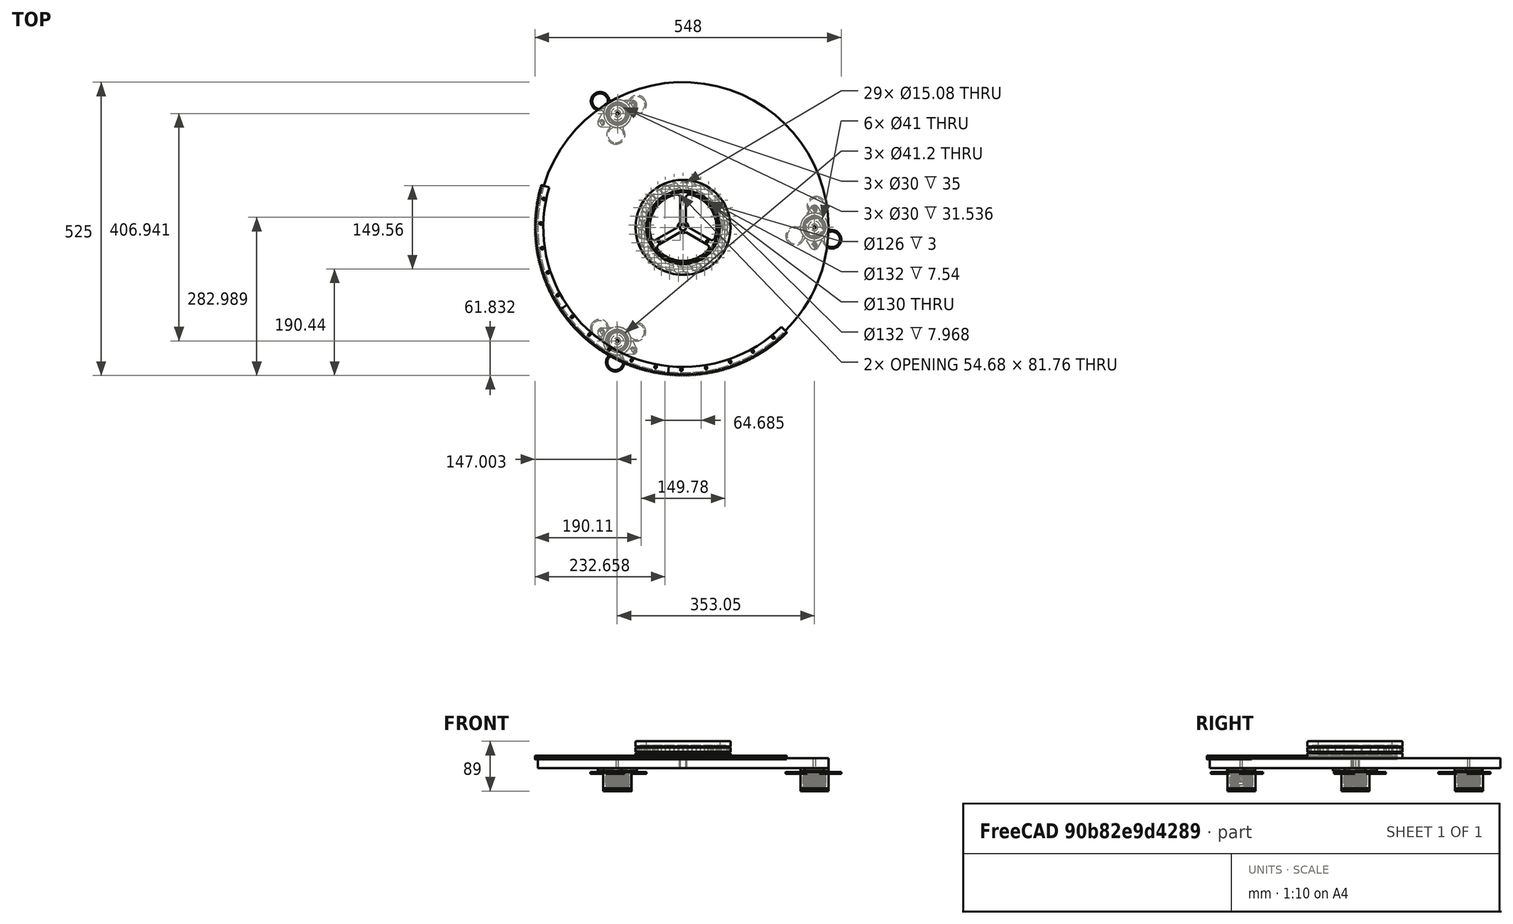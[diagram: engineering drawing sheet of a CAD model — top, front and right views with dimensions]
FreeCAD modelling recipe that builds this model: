
FCSTD DOCUMENT  (FreeCAD 2020.12.13R23076 +3015 (Git))
Label: zawieszenie-dol
License: All rights reserved
LicenseURL: http://en.wikipedia.org/wiki/All_rights_reserved
objects: App::FeaturePython×64, Part::FeaturePython×34, App::Link×12, App::LinkElement×6
note: 33 computed .brp shape members not serialized (recipe doc carries the construction recipe); baked Part::Feature solids carry a one-line shape summary decoded from their .brp
EXTERNAL_REF file=plyta-okr-dol.fcstd obj=Body
EXTERNAL_REF file=stopa.fcstd obj=Body
EXTERNAL_REF file=wieniec_mod1.FCStd obj=Body
EXTERNAL_REF file=tulejka-sruby.FCStd obj=Body
EXTERNAL_REF file=piasta-lozyska.FCStd obj=Body
EXTERNAL_REF file=lozysko 51126.FCStd obj=Assembly
EXTERNAL_REF file=regulacja-nogi.FCStd obj=Assembly

FEATURE [App::Link] Link  label="Link_plyta-okr-dol"
  LinkedObject = -> <external plyta-okr-dol.fcstd>#Body
  SyncGroupVisibility = false
  _LinkVersion = 1
FEATURE [App::Link] Link001  label="Link001_Assembly"
  LinkedObject = -> Assembly
  SyncGroupVisibility = false
  _LinkVersion = 1
FEATURE [App::Link] Link002  label="Link002_stopa"
  LinkPlacement = pos=(235,0,0) rot=(0,0,1;0rad)
  LinkedObject = -> <external stopa.fcstd>#Body
  Placement = pos=(235,0,0) rot=(0,0,1;0rad)
  SyncGroupVisibility = false
  _LinkVersion = 1
FEATURE [App::Link] Link003  label="Link003_Assembly"
  LinkedObject = -> Assembly
  SyncGroupVisibility = false
  _LinkVersion = 1
FEATURE [App::Link] Link004  label="Link004_Assembly"
  LinkedObject = -> Assembly
  SyncGroupVisibility = false
  _LinkVersion = 1
FEATURE [App::Link] Link005  label="Link005_stopa"
  LinkPlacement = pos=(-117.5,203.516,0) rot=(0,0,1;0rad)
  LinkedObject = -> <external stopa.fcstd>#Body
  Placement = pos=(-117.5,203.516,0) rot=(0,0,1;0rad)
  SyncGroupVisibility = false
  _LinkVersion = 1
FEATURE [App::Link] Link006  label="Link006_stopa"
  LinkPlacement = pos=(-117.5,-203.516,0) rot=(0,0,1;0rad)
  LinkedObject = -> <external stopa.fcstd>#Body
  Placement = pos=(-117.5,-203.516,0) rot=(0,0,1;0rad)
  SyncGroupVisibility = false
  _LinkVersion = 1
FEATURE [App::Link] Link008  label="tulejka-sruby"
  LinkPlacement = pos=(0,0,-4.40707e-10) rot=(0,0,1;0rad)
  LinkedObject = -> <external tulejka-sruby.FCStd>#Body
  Placement = pos=(0,0,-4.40707e-10) rot=(0,0,1;0rad)
  SyncGroupVisibility = false
  _LinkVersion = 1
FEATURE [App::Link] Link009  label="piasta-lozyska"
  LinkPlacement = pos=(0,0,18) rot=(0,0,1;0rad)
  LinkedObject = -> <external piasta-lozyska.FCStd>#Body
  Placement = pos=(0,0,18) rot=(0,0,1;0rad)
  SyncGroupVisibility = false
  _LinkVersion = 1
FEATURE [App::Link] Link010  label="51126-lozysko"
  LinkPlacement = pos=(0,0,18) rot=(0,-1,0;1.5708rad)
  LinkedObject = -> <external lozysko 51126.FCStd>#Assembly
  Placement = pos=(0,0,18) rot=(0,-1,0;1.5708rad)
  SyncGroupVisibility = false
  _LinkVersion = 1
FEATURE [App::LinkElement] Link011_i0
  LinkPlacement = pos=(0,0,1.8261e-12) rot=(0,0,1;0rad)
  LinkedObject = -> <external regulacja-nogi.FCStd>#Assembly
  Placement = pos=(0,0,1.8261e-12) rot=(0,0,1;0rad)
  _LinkVersion = 1
FEATURE [App::LinkElement] Link011_i1
  LinkPlacement = pos=(-203.516,-352.5,1.8296e-12) rot=(0,0,-1;1.0472rad)
  LinkedObject = -> <external regulacja-nogi.FCStd>#Assembly
  Placement = pos=(-203.516,-352.5,1.8296e-12) rot=(0,0,-1;1.0472rad)
  _LinkVersion = 1
FEATURE [App::LinkElement] Link011_i2
  LinkPlacement = pos=(203.516,-352.5,1.8296e-12) rot=(0,0,1;1.0472rad)
  LinkedObject = -> <external regulacja-nogi.FCStd>#Assembly
  Placement = pos=(203.516,-352.5,1.8296e-12) rot=(0,0,1;1.0472rad)
  _LinkVersion = 1
FEATURE [App::Link] Link011  label="regulacja-nogi"
  ElementCount = 3
  ElementList = -> [Link011_i0,Link011_i1,Link011_i2]
  LinkPlacement = pos=(235,0,-20) rot=(0.707107,0.707107,0;3.14159rad)
  LinkedObject = -> <external regulacja-nogi.FCStd>#Assembly
  Placement = pos=(235,0,-20) rot=(0.707107,0.707107,0;3.14159rad)
  SyncGroupVisibility = false
  _LinkVersion = 1
FEATURE [App::LinkElement] Link007_i0
  LinkPlacement = pos=(0,0,-3.6e-15) rot=(0,0,-1;5.65256rad)
  LinkedObject = -> <external wieniec_mod1.FCStd>#Body
  Placement = pos=(0,0,-3.6e-15) rot=(0,0,-1;5.65256rad)
  _LinkVersion = 0
FEATURE [App::LinkElement] Link007_i1
  LinkPlacement = pos=(2e-16,8e-16,3.6e-15) rot=(0,0,-1;4.77196rad)
  LinkedObject = -> <external wieniec_mod1.FCStd>#Body
  Placement = pos=(2e-16,8e-16,3.6e-15) rot=(0,0,-1;4.77196rad)
  _LinkVersion = 0
FEATURE [App::LinkElement] Link007_i2
  LinkPlacement = pos=(-1.93e-14,2.3e-15,2.49e-14) rot=(0,0,-1;0.249973rad)
  LinkedObject = -> <external wieniec_mod1.FCStd>#Body
  Placement = pos=(-1.93e-14,2.3e-15,2.49e-14) rot=(0,0,-1;0.249973rad)
  _LinkVersion = 0
FEATURE [App::Link] Link007  label="wieniec"
  ElementCount = 3
  ElementList = -> [Link007_i0,Link007_i1,Link007_i2]
  LinkPlacement = pos=(0,0,22) rot=(0.991445,-0.130526,0;3.14159rad)
  LinkedObject = -> <external wieniec_mod1.FCStd>#Body
  Placement = pos=(0,0,22) rot=(0.991445,-0.130526,0;3.14159rad)
  SyncGroupVisibility = false
  _LinkVersion = 1
FEATURE [Part::FeaturePython] Parts  # WARN: FeaturePython — macro-defined, semantics opaque (R4)
  Group = -> [Link,Link002,Link005,Link006,Link007,Link008,Link009,Link010,Link011]
  GroupMode = 0
  _LinkVersion = 1
FEATURE [Part::FeaturePython] Assembly  label="zawieszenie-dol"  # WARN: FeaturePython — macro-defined, semantics opaque (R4)
  AutoRelax = true
  BuildShape = 0
  Freeze = true
  Group = -> [Constraints,Elements,Parts]
  Verbose = false
  _LinkVersion = 1
  _SolverType = 1
FEATURE [App::FeaturePython] Constraints  # WARN: FeaturePython — macro-defined, semantics opaque (R4)
  Group = -> [Constraint001,Constraint002,Constraint003,Constraint004,Constraint005,Constraint006,Constraint,Constraint011,Constraint012,Constraint013,Constraint014,Constraint015,Constraint016,Constraint017,Constraint018,Constraint019,Constraint020,Constraint021,Constraint022,Constraint023,Constraint024]
  _LinkVersion = 1
  _Version = 1
FEATURE [App::FeaturePython] Elements  # WARN: FeaturePython — macro-defined, semantics opaque (R4)
  Group = -> [_Element,_Element001,_Element002,_Element003,_Element004,_Element005,_Element006,_Element007,_Element008,_Element009,_Element011,_Element013,_Element015,_Element017,Element,Element001,_Element018,_Element019,_Element020,_Element021,_Element022,_Element023,_Element024,_Element025,_Element026,_Element027,_Element028,_Element029,_Element030,_Element031,_Element032,_Element033]
  _LinkVersion = 1
FEATURE [Part::FeaturePython] _Element  # link proxy (typed FeaturePython)
  Detach = false
  LinkTransform = true
  LinkedObject = -> Link [PolarPattern.Face2]
  _LinkVersion = 1
  _Parent = -> Elements
FEATURE [App::FeaturePython] Constraint001  label="AxialAlignment"  # WARN: FeaturePython — macro-defined, semantics opaque (R4)
  Angle = 0
  AnglePitch = 0
  AngleRoll = 0
  Disabled = false
  Group = -> [ElementLink001,ElementLink002]
  LockAngle = false
  Multiply = false
  _ConstraintType = 36
  _LinkVersion = 1
  _Parent = -> Constraints
FEATURE [App::FeaturePython] ElementLink001  label="_Element001"  # link proxy (typed FeaturePython)
  LinkTransform = true
  LinkedObject = -> _Element001
  _LinkVersion = 1
  _Parent = -> Constraint001
FEATURE [Part::FeaturePython] _Element001  # link proxy (typed FeaturePython)
  Detach = false
  LinkTransform = true
  LinkedObject = -> Link005 [Revolution.Edge1]
  _LinkVersion = 1
  _Parent = -> Elements
FEATURE [App::FeaturePython] ElementLink002  label="_Element002"  # link proxy (typed FeaturePython)
  LinkTransform = true
  LinkedObject = -> _Element002
  _LinkVersion = 1
  _Parent = -> Constraint001
FEATURE [Part::FeaturePython] _Element002  # link proxy (typed FeaturePython)
  Detach = false
  LinkTransform = true
  LinkedObject = -> Link [PolarPattern.Edge6]
  _LinkVersion = 1
  _Parent = -> Elements
FEATURE [App::FeaturePython] Constraint002  label="PlaneAlignment"  # WARN: FeaturePython — macro-defined, semantics opaque (R4)
  Angle = 0
  AnglePitch = 0
  AngleRoll = 0
  Cascade = false
  Disabled = false
  Group = -> [ElementLink003,ElementLink004]
  LockAngle = false
  _ConstraintType = 37
  _LinkVersion = 1
  _Parent = -> Constraints
FEATURE [App::FeaturePython] ElementLink003  label="_Element"  # link proxy (typed FeaturePython)
  LinkTransform = true
  LinkedObject = -> _Element
  _LinkVersion = 1
  _Parent = -> Constraint002
FEATURE [App::FeaturePython] ElementLink004  label="_Element003"  # link proxy (typed FeaturePython)
  LinkTransform = true
  LinkedObject = -> _Element003
  _LinkVersion = 1
  _Parent = -> Constraint002
FEATURE [Part::FeaturePython] _Element003  # link proxy (typed FeaturePython)
  Detach = false
  LinkTransform = true
  LinkedObject = -> Link005 [Revolution.Face1]
  _LinkVersion = 1
  _Parent = -> Elements
FEATURE [App::FeaturePython] Constraint003  label="AxialAlignment001"  # WARN: FeaturePython — macro-defined, semantics opaque (R4)
  Angle = 0
  AnglePitch = 0
  AngleRoll = 0
  Disabled = false
  Group = -> [ElementLink005,ElementLink006]
  LockAngle = false
  Multiply = false
  _ConstraintType = 36
  _LinkVersion = 1
  _Parent = -> Constraints
FEATURE [App::FeaturePython] ElementLink005  label="_Element004"  # link proxy (typed FeaturePython)
  LinkTransform = true
  LinkedObject = -> _Element004
  _LinkVersion = 1
  _Parent = -> Constraint003
FEATURE [Part::FeaturePython] _Element004  # link proxy (typed FeaturePython)
  Detach = false
  LinkTransform = true
  LinkedObject = -> Link006 [Revolution.Edge1]
  _LinkVersion = 1
  _Parent = -> Elements
FEATURE [App::FeaturePython] ElementLink006  label="_Element005"  # link proxy (typed FeaturePython)
  LinkTransform = true
  LinkedObject = -> _Element005
  _LinkVersion = 1
  _Parent = -> Constraint003
FEATURE [Part::FeaturePython] _Element005  # link proxy (typed FeaturePython)
  Detach = false
  LinkTransform = true
  LinkedObject = -> Link [PolarPattern.Edge4]
  _LinkVersion = 1
  _Parent = -> Elements
FEATURE [App::FeaturePython] Constraint004  label="PlaneAlignment001"  # WARN: FeaturePython — macro-defined, semantics opaque (R4)
  Angle = 0
  AnglePitch = 0
  AngleRoll = 0
  Cascade = false
  Disabled = false
  Group = -> [ElementLink007,ElementLink008]
  LockAngle = false
  _ConstraintType = 37
  _LinkVersion = 1
  _Parent = -> Constraints
FEATURE [App::FeaturePython] ElementLink007  label="_Element"  # link proxy (typed FeaturePython)
  LinkTransform = true
  LinkedObject = -> _Element
  _LinkVersion = 1
  _Parent = -> Constraint004
FEATURE [App::FeaturePython] ElementLink008  label="_Element006"  # link proxy (typed FeaturePython)
  LinkTransform = true
  LinkedObject = -> _Element006
  _LinkVersion = 1
  _Parent = -> Constraint004
FEATURE [Part::FeaturePython] _Element006  # link proxy (typed FeaturePython)
  Detach = false
  LinkTransform = true
  LinkedObject = -> Link006 [Revolution.Face1]
  _LinkVersion = 1
  _Parent = -> Elements
FEATURE [App::FeaturePython] Constraint005  label="AxialAlignment002"  # WARN: FeaturePython — macro-defined, semantics opaque (R4)
  Angle = 0
  AnglePitch = 0
  AngleRoll = 0
  Disabled = false
  Group = -> [ElementLink009,ElementLink010]
  LockAngle = false
  Multiply = false
  _ConstraintType = 36
  _LinkVersion = 1
  _Parent = -> Constraints
FEATURE [App::FeaturePython] ElementLink009  label="_Element007"  # link proxy (typed FeaturePython)
  LinkTransform = true
  LinkedObject = -> _Element007
  _LinkVersion = 1
  _Parent = -> Constraint005
FEATURE [Part::FeaturePython] _Element007  # link proxy (typed FeaturePython)
  Detach = false
  LinkTransform = true
  LinkedObject = -> Link002 [Revolution.Edge1]
  _LinkVersion = 1
  _Parent = -> Elements
FEATURE [App::FeaturePython] ElementLink010  label="_Element008"  # link proxy (typed FeaturePython)
  LinkTransform = true
  LinkedObject = -> _Element008
  _LinkVersion = 1
  _Parent = -> Constraint005
FEATURE [Part::FeaturePython] _Element008  # link proxy (typed FeaturePython)
  Detach = false
  LinkTransform = true
  LinkedObject = -> Link [PolarPattern.Edge5]
  _LinkVersion = 1
  _Parent = -> Elements
FEATURE [App::FeaturePython] Constraint006  label="PlaneAlignment002"  # WARN: FeaturePython — macro-defined, semantics opaque (R4)
  Angle = 0
  AnglePitch = 0
  AngleRoll = 0
  Cascade = false
  Disabled = false
  Group = -> [ElementLink011,ElementLink012]
  LockAngle = false
  _ConstraintType = 37
  _LinkVersion = 1
  _Parent = -> Constraints
FEATURE [App::FeaturePython] ElementLink011  label="_Element"  # link proxy (typed FeaturePython)
  LinkTransform = true
  LinkedObject = -> _Element
  _LinkVersion = 1
  _Parent = -> Constraint006
FEATURE [App::FeaturePython] ElementLink012  label="_Element009"  # link proxy (typed FeaturePython)
  LinkTransform = true
  LinkedObject = -> _Element009
  _LinkVersion = 1
  _Parent = -> Constraint006
FEATURE [Part::FeaturePython] _Element009  # link proxy (typed FeaturePython)
  Detach = false
  LinkTransform = true
  LinkedObject = -> Link002 [Revolution.Face1]
  _LinkVersion = 1
  _Parent = -> Elements
FEATURE [Part::FeaturePython] _Element011  # link proxy (typed FeaturePython)
  Detach = false
  LinkTransform = true
  LinkedObject = -> Link [PolarPattern.Face1]
  _LinkVersion = 1
  _Parent = -> Elements
FEATURE [Part::FeaturePython] _Element013  # link proxy (typed FeaturePython)
  Detach = false
  LinkTransform = true
  LinkedObject = -> Link [PolarPattern.Face3]
  _LinkVersion = 1
  _Parent = -> Elements
FEATURE [Part::FeaturePython] _Element015  # link proxy (typed FeaturePython)
  Detach = false
  LinkTransform = true
  LinkedObject = -> Link [Pocket001.Face1]
  _LinkVersion = 1
  _Parent = -> Elements
FEATURE [Part::FeaturePython] _Element017  # link proxy (typed FeaturePython)
  Detach = false
  LinkTransform = true
  LinkedObject = -> Link [Pocket001.Face3]
  _LinkVersion = 1
  _Parent = -> Elements
FEATURE [Part::FeaturePython] Element  # link proxy (typed FeaturePython)
  Detach = false
  LinkTransform = true
  LinkedObject = -> Link [Pocket001.Face5]
  _LinkVersion = 1
  _Parent = -> Elements
FEATURE [Part::FeaturePython] Element001  # link proxy (typed FeaturePython)
  Detach = false
  LinkTransform = true
  LinkedObject = -> Link [Pocket001.Edge5]
  _LinkVersion = 1
  _Parent = -> Elements
FEATURE [App::FeaturePython] Constraint  label="Locked"  # WARN: FeaturePython — macro-defined, semantics opaque (R4)
  Disabled = false
  Group = -> [ElementLink]
  _ConstraintType = 0
  _LinkVersion = 1
  _Parent = -> Constraints
FEATURE [App::FeaturePython] ElementLink  label="_Element018"  # link proxy (typed FeaturePython)
  LinkTransform = true
  LinkedObject = -> _Element018
  _LinkVersion = 1
  _Parent = -> Constraint
FEATURE [Part::FeaturePython] _Element018  # link proxy (typed FeaturePython)
  Detach = false
  LinkTransform = true
  LinkedObject = -> Link [Pocket001.Face2]
  _LinkVersion = 1
  _Parent = -> Elements
FEATURE [Part::FeaturePython] _Element019  # link proxy (typed FeaturePython)
  Detach = false
  LinkTransform = true
  LinkedObject = -> Link008 [Chamfer.Face1]
  _LinkVersion = 1
  _Parent = -> Elements
FEATURE [Part::FeaturePython] _Element020  # link proxy (typed FeaturePython)
  Detach = false
  LinkTransform = true
  LinkedObject = -> Link008 [Chamfer.Face3]
  _LinkVersion = 1
  _Parent = -> Elements
FEATURE [App::FeaturePython] Constraint011  label="PlaneCoincident"  # WARN: FeaturePython — macro-defined, semantics opaque (R4)
  Angle = 0
  AnglePitch = 0
  AngleRoll = 0
  Cascade = false
  Disabled = false
  Group = -> [ElementLink021,ElementLink022]
  LockAngle = false
  Multiply = false
  OffsetX = 0
  OffsetY = 0
  _ConstraintType = 35
  _LinkVersion = 1
  _Parent = -> Constraints
FEATURE [App::FeaturePython] ElementLink021  label="_Element021"  # link proxy (typed FeaturePython)
  LinkTransform = true
  LinkedObject = -> _Element021
  _LinkVersion = 1
  _Parent = -> Constraint011
FEATURE [Part::FeaturePython] _Element021  # link proxy (typed FeaturePython)
  Detach = false
  LinkTransform = true
  LinkedObject = -> Link009 [Pocket002.Face1]
  _LinkVersion = 1
  _Parent = -> Elements
FEATURE [App::FeaturePython] ElementLink022  label="_Element017"  # link proxy (typed FeaturePython)
  LinkTransform = true
  LinkedObject = -> _Element017
  _LinkVersion = 1
  _Parent = -> Constraint011
FEATURE [App::FeaturePython] Constraint012  label="PlaneCoincident001"  # WARN: FeaturePython — macro-defined, semantics opaque (R4)
  Angle = 0
  AnglePitch = 0
  AngleRoll = 0
  Cascade = false
  Disabled = false
  Group = -> [ElementLink023,ElementLink024]
  LockAngle = false
  Multiply = false
  OffsetX = 0
  OffsetY = 0
  _ConstraintType = 35
  _LinkVersion = 1
  _Parent = -> Constraints
FEATURE [App::FeaturePython] ElementLink023  label="_Element020"  # link proxy (typed FeaturePython)
  LinkTransform = true
  LinkedObject = -> _Element020
  _LinkVersion = 1
  _Parent = -> Constraint012
FEATURE [App::FeaturePython] ElementLink024  label="_Element018"  # link proxy (typed FeaturePython)
  LinkTransform = true
  LinkedObject = -> _Element018
  _LinkVersion = 1
  _Parent = -> Constraint012
FEATURE [App::FeaturePython] Constraint013  label="PlaneCoincident002"  # WARN: FeaturePython — macro-defined, semantics opaque (R4)
  Angle = 0
  AnglePitch = 0
  AngleRoll = 0
  Cascade = false
  Disabled = false
  Group = -> [ElementLink025,ElementLink026]
  LockAngle = false
  Multiply = false
  OffsetX = 0
  OffsetY = 0
  _ConstraintType = 35
  _LinkVersion = 1
  _Parent = -> Constraints
FEATURE [App::FeaturePython] ElementLink025  label="_Element022"  # link proxy (typed FeaturePython)
  LinkTransform = true
  LinkedObject = -> _Element022
  _LinkVersion = 1
  _Parent = -> Constraint013
FEATURE [Part::FeaturePython] _Element022  # link proxy (typed FeaturePython)
  Detach = false
  LinkTransform = true
  LinkedObject = -> Link010 [1.$Element.]
  _LinkVersion = 1
  _Parent = -> Elements
FEATURE [App::FeaturePython] ElementLink026  label="_Element017"  # link proxy (typed FeaturePython)
  LinkTransform = true
  LinkedObject = -> _Element017
  _LinkVersion = 1
  _Parent = -> Constraint013
FEATURE [Part::FeaturePython] _Element023  # link proxy (typed FeaturePython)
  Detach = false
  LinkTransform = true
  LinkedObject = -> Link [Pocket001.Edge6]
  _LinkVersion = 1
  _Parent = -> Elements
FEATURE [App::FeaturePython] Constraint014  label="PlaneCoincident003"  # WARN: FeaturePython — macro-defined, semantics opaque (R4)
  Angle = 0
  AnglePitch = 0
  AngleRoll = 0
  Cascade = false
  Disabled = false
  Group = -> [ElementLink027,ElementLink028]
  LockAngle = false
  Multiply = false
  OffsetX = 0
  OffsetY = 0
  _ConstraintType = 35
  _LinkVersion = 1
  _Parent = -> Constraints
FEATURE [App::FeaturePython] ElementLink027  label="_Element024"  # link proxy (typed FeaturePython)
  LinkTransform = true
  LinkedObject = -> _Element024
  _LinkVersion = 1
  _Parent = -> Constraint014
FEATURE [Part::FeaturePython] _Element024  # link proxy (typed FeaturePython)
  Detach = false
  LinkTransform = true
  LinkedObject = -> Link011 [0.1.$Element002.]
  _LinkVersion = 1
  _Parent = -> Elements
FEATURE [App::FeaturePython] ElementLink028  label="_Element009"  # link proxy (typed FeaturePython)
  LinkTransform = true
  LinkedObject = -> _Element009
  _LinkVersion = 1
  _Parent = -> Constraint014
FEATURE [App::FeaturePython] Constraint015  label="PlaneCoincident004"  # WARN: FeaturePython — macro-defined, semantics opaque (R4)
  Angle = 0
  AnglePitch = 0
  AngleRoll = 0
  Cascade = false
  Disabled = false
  Group = -> [ElementLink029,ElementLink030]
  LockAngle = false
  Multiply = false
  OffsetX = 0
  OffsetY = 0
  _ConstraintType = 35
  _LinkVersion = 1
  _Parent = -> Constraints
FEATURE [App::FeaturePython] ElementLink029  label="_Element025"  # link proxy (typed FeaturePython)
  LinkTransform = true
  LinkedObject = -> _Element025
  _LinkVersion = 1
  _Parent = -> Constraint015
FEATURE [Part::FeaturePython] _Element025  # link proxy (typed FeaturePython)
  Detach = false
  LinkTransform = true
  LinkedObject = -> Link011 [2.1.$Element002.]
  _LinkVersion = 1
  _Parent = -> Elements
FEATURE [App::FeaturePython] ElementLink030  label="_Element003"  # link proxy (typed FeaturePython)
  LinkTransform = true
  LinkedObject = -> _Element003
  _LinkVersion = 1
  _Parent = -> Constraint015
FEATURE [App::FeaturePython] Constraint016  label="PlaneCoincident005"  # WARN: FeaturePython — macro-defined, semantics opaque (R4)
  Angle = 0
  AnglePitch = 0
  AngleRoll = 0
  Cascade = false
  Disabled = false
  Group = -> [ElementLink031,ElementLink032]
  LockAngle = false
  Multiply = false
  OffsetX = 0
  OffsetY = 0
  _ConstraintType = 35
  _LinkVersion = 1
  _Parent = -> Constraints
FEATURE [App::FeaturePython] ElementLink031  label="_Element006"  # link proxy (typed FeaturePython)
  LinkTransform = true
  LinkedObject = -> _Element006
  _LinkVersion = 1
  _Parent = -> Constraint016
FEATURE [App::FeaturePython] ElementLink032  label="_Element026"  # link proxy (typed FeaturePython)
  LinkTransform = true
  LinkedObject = -> _Element026
  _LinkVersion = 1
  _Parent = -> Constraint016
FEATURE [Part::FeaturePython] _Element026  # link proxy (typed FeaturePython)
  Detach = false
  LinkTransform = true
  LinkedObject = -> Link011 [1.1.$Element002.]
  _LinkVersion = 1
  _Parent = -> Elements
FEATURE [App::FeaturePython] Constraint017  label="AxialAlignment003"  # WARN: FeaturePython — macro-defined, semantics opaque (R4)
  Angle = 0
  AnglePitch = 0
  AngleRoll = 0
  Disabled = false
  Group = -> [ElementLink033,ElementLink034]
  LockAngle = false
  Multiply = false
  _ConstraintType = 36
  _LinkVersion = 0
  _Parent = -> Constraints
FEATURE [App::FeaturePython] ElementLink033  label="_Element027"  # link proxy (typed FeaturePython)
  LinkTransform = true
  LinkedObject = -> _Element027
  _LinkVersion = 0
  _Parent = -> Constraint017
FEATURE [Part::FeaturePython] _Element027  # link proxy (typed FeaturePython)
  Detach = false
  LinkTransform = true
  LinkedObject = -> Link007 [2.Pocket003.Face3]
  _LinkVersion = 0
  _Parent = -> Elements
FEATURE [App::FeaturePython] ElementLink034  label="_Element015"  # link proxy (typed FeaturePython)
  LinkTransform = true
  LinkedObject = -> _Element015
  _LinkVersion = 0
  _Parent = -> Constraint017
FEATURE [App::FeaturePython] Constraint018  label="AxialAlignment004"  # WARN: FeaturePython — macro-defined, semantics opaque (R4)
  Angle = 0
  AnglePitch = 0
  AngleRoll = 0
  Disabled = false
  Group = -> [ElementLink035,ElementLink036]
  LockAngle = false
  Multiply = false
  _ConstraintType = 36
  _LinkVersion = 0
  _Parent = -> Constraints
FEATURE [App::FeaturePython] ElementLink035  label="_Element028"  # link proxy (typed FeaturePython)
  LinkTransform = true
  LinkedObject = -> _Element028
  _LinkVersion = 0
  _Parent = -> Constraint018
FEATURE [Part::FeaturePython] _Element028  # link proxy (typed FeaturePython)
  Detach = false
  LinkTransform = true
  LinkedObject = -> Link007 [0.Pocket003.Face3]
  _LinkVersion = 0
  _Parent = -> Elements
FEATURE [App::FeaturePython] ElementLink036  label="_Element015"  # link proxy (typed FeaturePython)
  LinkTransform = true
  LinkedObject = -> _Element015
  _LinkVersion = 0
  _Parent = -> Constraint018
FEATURE [App::FeaturePython] Constraint019  label="PointInPlane"  # WARN: FeaturePython — macro-defined, semantics opaque (R4)
  Disabled = false
  Group = -> [ElementLink037,ElementLink038]
  _ConstraintType = 3
  _LinkVersion = 0
  _Parent = -> Constraints
FEATURE [App::FeaturePython] ElementLink037  label="_Element029"  # link proxy (typed FeaturePython)
  LinkTransform = true
  LinkedObject = -> _Element029
  _LinkVersion = 0
  _Parent = -> Constraint019
FEATURE [Part::FeaturePython] _Element029  # link proxy (typed FeaturePython)
  Detach = false
  LinkTransform = true
  LinkedObject = -> Link007 [0.Pocket003.Vertex323]
  _LinkVersion = 0
  _Parent = -> Elements
FEATURE [App::FeaturePython] ElementLink038  label="_Element017"  # link proxy (typed FeaturePython)
  LinkTransform = true
  LinkedObject = -> _Element017
  _LinkVersion = 0
  _Parent = -> Constraint019
FEATURE [App::FeaturePython] Constraint020  label="PointInPlane001"  # WARN: FeaturePython — macro-defined, semantics opaque (R4)
  Disabled = false
  Group = -> [ElementLink039,ElementLink040]
  _ConstraintType = 3
  _LinkVersion = 0
  _Parent = -> Constraints
FEATURE [App::FeaturePython] ElementLink039  label="_Element030"  # link proxy (typed FeaturePython)
  LinkTransform = true
  LinkedObject = -> _Element030
  _LinkVersion = 0
  _Parent = -> Constraint020
FEATURE [Part::FeaturePython] _Element030  # link proxy (typed FeaturePython)
  Detach = false
  LinkTransform = true
  LinkedObject = -> Link007 [2.Pocket003.Vertex325]
  _LinkVersion = 0
  _Parent = -> Elements
FEATURE [App::FeaturePython] ElementLink040  label="_Element017"  # link proxy (typed FeaturePython)
  LinkTransform = true
  LinkedObject = -> _Element017
  _LinkVersion = 0
  _Parent = -> Constraint020
FEATURE [App::FeaturePython] Constraint021  label="PointsCoincident"  # WARN: FeaturePython — macro-defined, semantics opaque (R4)
  Disabled = false
  Group = -> [ElementLink041,ElementLink042]
  _ConstraintType = 1
  _LinkVersion = 0
  _Parent = -> Constraints
FEATURE [App::FeaturePython] ElementLink041  label="_Element030"  # link proxy (typed FeaturePython)
  LinkTransform = true
  LinkedObject = -> _Element030
  _LinkVersion = 0
  _Parent = -> Constraint021
FEATURE [App::FeaturePython] ElementLink042  label="_Element029"  # link proxy (typed FeaturePython)
  LinkTransform = true
  LinkedObject = -> _Element029
  _LinkVersion = 0
  _Parent = -> Constraint021
FEATURE [App::FeaturePython] Constraint022  label="AxialAlignment005"  # WARN: FeaturePython — macro-defined, semantics opaque (R4)
  Angle = 0
  AnglePitch = 0
  AngleRoll = 0
  Disabled = false
  Group = -> [ElementLink043,ElementLink044]
  LockAngle = false
  Multiply = false
  _ConstraintType = 36
  _LinkVersion = 0
  _Parent = -> Constraints
FEATURE [App::FeaturePython] ElementLink043  label="_Element031"  # link proxy (typed FeaturePython)
  LinkTransform = true
  LinkedObject = -> _Element031
  _LinkVersion = 0
  _Parent = -> Constraint022
FEATURE [Part::FeaturePython] _Element031  # link proxy (typed FeaturePython)
  Detach = false
  LinkTransform = true
  LinkedObject = -> Link007 [1.Pocket003.Face3]
  _LinkVersion = 0
  _Parent = -> Elements
FEATURE [App::FeaturePython] ElementLink044  label="_Element015"  # link proxy (typed FeaturePython)
  LinkTransform = true
  LinkedObject = -> _Element015
  _LinkVersion = 0
  _Parent = -> Constraint022
FEATURE [App::FeaturePython] Constraint023  label="PointInPlane002"  # WARN: FeaturePython — macro-defined, semantics opaque (R4)
  Disabled = false
  Group = -> [ElementLink045,ElementLink046]
  _ConstraintType = 3
  _LinkVersion = 0
  _Parent = -> Constraints
FEATURE [App::FeaturePython] ElementLink045  label="_Element032"  # link proxy (typed FeaturePython)
  LinkTransform = true
  LinkedObject = -> _Element032
  _LinkVersion = 0
  _Parent = -> Constraint023
FEATURE [Part::FeaturePython] _Element032  # link proxy (typed FeaturePython)
  Detach = false
  LinkTransform = true
  LinkedObject = -> Link007 [1.Pocket003.Vertex323]
  _LinkVersion = 0
  _Parent = -> Elements
FEATURE [App::FeaturePython] ElementLink046  label="_Element017"  # link proxy (typed FeaturePython)
  LinkTransform = true
  LinkedObject = -> _Element017
  _LinkVersion = 0
  _Parent = -> Constraint023
FEATURE [App::FeaturePython] Constraint024  label="PointsCoincident001"  # WARN: FeaturePython — macro-defined, semantics opaque (R4)
  Disabled = false
  Group = -> [ElementLink047,ElementLink048]
  _ConstraintType = 1
  _LinkVersion = 0
  _Parent = -> Constraints
FEATURE [App::FeaturePython] ElementLink047  label="_Element032"  # link proxy (typed FeaturePython)
  LinkTransform = true
  LinkedObject = -> _Element032
  _LinkVersion = 0
  _Parent = -> Constraint024
FEATURE [App::FeaturePython] ElementLink048  label="_Element033"  # link proxy (typed FeaturePython)
  LinkTransform = true
  LinkedObject = -> _Element033
  _LinkVersion = 0
  _Parent = -> Constraint024
FEATURE [Part::FeaturePython] _Element033  # link proxy (typed FeaturePython)
  Detach = false
  LinkTransform = true
  LinkedObject = -> Link007 [0.Pocket003.Vertex325]
  _LinkVersion = 0
  _Parent = -> Elements

RESOLVED EXTERNAL PARTS (link-assembly join: the EXTERNAL_REF files above that resolve inside this repo's crawl, each included once):
---- part piasta-lozyska.FCStd = doc fcstd_be0ec29206c3 ----
FCSTD DOCUMENT  (FreeCAD 2020.10.16R22739 +2665 (Git))
Label: piasta-lozyska
License: All rights reserved
LicenseURL: http://en.wikipedia.org/wiki/All_rights_reserved
objects: Sketcher::SketchObject×4, PartDesign::Pocket×3, PartDesign::Pad×1, PartDesign::PolarPattern×1, PartDesign::Chamfer×1, PartDesign::Fillet×1, PartDesign::Body×1
note: 25 computed .brp shape members not serialized (recipe doc carries the construction recipe); baked Part::Feature solids carry a one-line shape summary decoded from their .brp

FEATURE [Sketcher::SketchObject] Sketch002
  MapMode = 5
  Support = -> [XY_Plane]
  sketch-geometry (7):
    g0: ArcOfCircle CenterX=0 CenterY=0 CenterZ=0 NormalX=0 NormalY=0 NormalZ=1 AngleXU=0 Radius=60 StartAngle=1.65423 EndAngle=3.58176
    g1: ArcOfCircle CenterX=0 CenterY=0 CenterZ=0 NormalX=0 NormalY=0 NormalZ=1 AngleXU=0 Radius=10 StartAngle=2.0944 EndAngle=3.14159
    g2: LineSegment StartX=-5 StartY=8.66025 StartZ=0 EndX=-5 EndY=59.7913 EndZ=0
    g3: LineSegment [constr] StartX=0 StartY=0 StartZ=0 EndX=-86.6025 EndY=-50 EndZ=0
    g4: LineSegment StartX=-10 StartY=-1e-16 StartZ=0 EndX=-54.2808 EndY=-25.5655 EndZ=0
    g5: LineSegment [constr] StartX=-10 StartY=-1e-16 StartZ=0 EndX=0 EndY=0 EndZ=0
    g6: Circle CenterX=0 CenterY=50 CenterZ=0 NormalX=0 NormalY=0 NormalZ=1 AngleXU=0 Radius=2
  constraints (20):
    c: Coincident(g0,g-1)
    c: Coincident(g1,g0)
    c: Vertical(g2)
    c: Coincident(g3,g0)
    c: Angle(g3) = -2.61799
    c: Parallel(g4,g3)
    c: Diameter(g0) = 120
    c: Coincident(g5,g4)
    c: Coincident(g5,g0)
    c: Coincident(g0,g2)
    c: Coincident(g0,g4)
    c: Coincident(g1,g2)
    c: DistanceX(g1) = -5
    c: Diameter(g1) = 20
    c: Distance(g1,g3) = 5
    c: Coincident(g4,g1)
    c: Distance(g3) = 100
    c: PointOnObject(g6,g-2)
    c: Diameter(g6) = 4
    c: DistanceY(g6) = 50
FEATURE [Sketcher::SketchObject] Sketch001
  MapMode = 5
  Support = -> [XY_Plane]
  sketch-geometry (1):
    g0: Circle CenterX=0 CenterY=0 CenterZ=0 NormalX=0 NormalY=0 NormalZ=1 AngleXU=0 Radius=5.5
  constraints (2):
    c: Coincident(g0,g-1)
    c: Diameter(g0) = 11
FEATURE [Sketcher::SketchObject] Sketch
  MapMode = 5
  Support = -> [XY_Plane]
  sketch-geometry (1):
    g0: Circle CenterX=0 CenterY=0 CenterZ=0 NormalX=0 NormalY=0 NormalZ=1 AngleXU=0 Radius=65.25
  constraints (2):
    c: Coincident(g0,g-1)
    c: Diameter(g0) = 130.5
FEATURE [PartDesign::Pad] Pad
  ClaimChildren = false
  Direction = (1,1,1)
  Length = 6
  Length2 = 100
  NewSolid = false
  Profile = -> Sketch
  Suppress = false
  Type = 0
FEATURE [PartDesign::Pocket] Pocket
  BaseFeature = -> Pad
  ClaimChildren = false
  Length = 5
  Length2 = 100
  NewSolid = false
  Profile = -> Sketch001
  Reversed = true
  Suppress = false
  Type = 1
FEATURE [PartDesign::Pocket] Pocket001
  BaseFeature = -> Pocket
  ClaimChildren = false
  Length = 5
  Length2 = 100
  NewSolid = false
  Profile = -> Sketch002
  Reversed = true
  Suppress = false
  Type = 1
FEATURE [PartDesign::PolarPattern] PolarPattern
  Angle = 360
  Axis = -> Sketch002 [N_Axis]
  BaseFeature = -> Pocket001
  CopyShape = false
  NewSolid = false
  Occurrences = 3
  OriginalSubs = -> [Pocket001]
  Originals = -> [Pocket001]
  SubTransform = true
  Suppress = false
FEATURE [PartDesign::Chamfer] Chamfer
  Angle = 45
  Base = -> PolarPattern [Edge3,Edge2]
  BaseFeature = -> PolarPattern
  ChamferType = 0
  FlipDirection = false
  NewSolid = false
  Size = 1
  Size2 = 1
  SupportTransform = true
  Suppress = false
FEATURE [PartDesign::Fillet] Fillet
  Base = -> Chamfer [Edge49,Edge46,Edge54,Edge52,Edge42,Edge40]
  BaseFeature = -> Chamfer
  NewSolid = false
  Radius = 6
  SupportTransform = true
  Suppress = false
FEATURE [Sketcher::SketchObject] Sketch003
  MapMode = 5
  Placement = pos=(0,0,6) rot=(0,0,1;0rad)
  Support = -> [Fillet]
  sketch-geometry (1):
    g0: Circle CenterX=0 CenterY=0 CenterZ=0 NormalX=0 NormalY=0 NormalZ=1 AngleXU=0 Radius=63
  constraints (2):
    c: Coincident(g0,g-1)
    c: Diameter(g0) = 126
FEATURE [PartDesign::Pocket] Pocket002
  BaseFeature = -> Fillet
  ClaimChildren = false
  Length = 3
  Length2 = 100
  NewSolid = false
  Profile = -> Sketch003
  Suppress = false
  Type = 0
FEATURE [PartDesign::Body] Body  label="piasta-lozyska"
  ExportMode = 0
  Group = -> [Sketch,Pad,Sketch001,Pocket,Sketch002,Pocket001,PolarPattern,Chamfer,Fillet,Sketch003,Pocket002]
  Origin = -> Origin
  Tip = -> Pocket002
  _ExportChildren = -> [Pad,Pocket,Pocket001,PolarPattern,Chamfer,Fillet,Pocket002]
  _GroupVersion = 1
---- part plyta-okr-dol.fcstd = doc fcstd_a5daffcc101f ----
FCSTD DOCUMENT  (FreeCAD 2020.12.13R23076 +3015 (Git))
Label: plyta-okr-dol
License: All rights reserved
LicenseURL: http://en.wikipedia.org/wiki/All_rights_reserved
objects: Sketcher::SketchObject×3, PartDesign::Pocket×2, PartDesign::Pad×1, PartDesign::PolarPattern×1, PartDesign::Body×1
note: 15 computed .brp shape members not serialized (recipe doc carries the construction recipe); baked Part::Feature solids carry a one-line shape summary decoded from their .brp

FEATURE [Sketcher::SketchObject] Sketch
  MapMode = 5
  Support = -> [XY_Plane]
  sketch-geometry (1):
    g0: Circle CenterX=0 CenterY=0 CenterZ=0 NormalX=0 NormalY=0 NormalZ=1 AngleXU=0 Radius=260
  constraints (2):
    c: Coincident(g0,g-1)
    c: Diameter(g0) = 520
FEATURE [PartDesign::Pad] Pad
  AllowMultiFace = false
  ClaimChildren = false
  Direction = (1,1,1)
  Fit = 0
  FitJoin = 0
  InnerFit = 0
  InnerFitJoin = 0
  InnerTaperAngle = 0
  InnerTaperAngleRev = 0
  Length = 18
  Length2 = 100
  NewSolid = false
  Profile = -> Sketch
  Suppress = false
  Type = 0
FEATURE [Sketcher::SketchObject] Sketch001
  MapMode = 5
  Placement = pos=(0,0,18) rot=(0,0,1;0rad)
  Support = -> [Pad]
  sketch-geometry (1):
    g0: Circle CenterX=235 CenterY=0 CenterZ=0 NormalX=0 NormalY=0 NormalZ=1 AngleXU=0 Radius=2
  constraints (3):
    c: PointOnObject(g0,g-1)
    c: DistanceX(g0) = 235
    c: Radius(g0) = 2
FEATURE [PartDesign::Pocket] Pocket
  AllowMultiFace = false
  BaseFeature = -> Pad
  ClaimChildren = false
  Fit = 0
  FitJoin = 0
  InnerFit = 0
  InnerFitJoin = 0
  InnerTaperAngle = 0
  InnerTaperAngleRev = 0
  Length = 5
  Length2 = 100
  NewSolid = false
  Profile = -> Sketch001
  Suppress = false
  Type = 1
FEATURE [PartDesign::PolarPattern] PolarPattern
  Angle = 360
  Axis = -> Sketch001 [N_Axis]
  BaseFeature = -> Pocket
  CopyShape = true
  NewSolid = false
  Occurrences = 3
  OriginalSubs = -> [Pocket]
  Originals = -> [Pocket]
  SubTransform = true
  Suppress = false
FEATURE [Sketcher::SketchObject] Sketch002
  MapMode = 5
  Support = -> [XY_Plane]
  sketch-geometry (1):
    g0: Circle CenterX=0 CenterY=0 CenterZ=0 NormalX=0 NormalY=0 NormalZ=1 AngleXU=0 Radius=7
  constraints (2):
    c: Coincident(g0,g-1)
    c: Diameter(g0) = 14
FEATURE [PartDesign::Pocket] Pocket001
  BaseFeature = -> PolarPattern
  ClaimChildren = false
  Fit = 0
  FitJoin = 0
  InnerFit = 0
  InnerFitJoin = 0
  InnerTaperAngle = 0
  InnerTaperAngleRev = 0
  Length = 5
  Length2 = 100
  NewSolid = false
  Profile = -> Sketch002
  Reversed = true
  Suppress = false
  Type = 1
FEATURE [PartDesign::Body] Body  label="plyta-okr-dol"
  ExportMode = 0
  Group = -> [Sketch,Pad,Sketch001,Pocket,PolarPattern,Sketch002,Pocket001]
  Origin = -> Origin
  SingleSolid = true
  Tip = -> Pocket001
  _ExportChildren = -> [Pad,Pocket,PolarPattern,Pocket001]
  _GroupVersion = 1
---- part regulacja-nogi.FCStd = doc fcstd_2b6e49dfca54 ----
FCSTD DOCUMENT  (FreeCAD 2020.11.29R23076 +2859 (Git))
Label: regulacja-nogi
License: All rights reserved
LicenseURL: http://en.wikipedia.org/wiki/All_rights_reserved
objects: App::FeaturePython×13, Part::FeaturePython×11, App::Link×3
note: 10 computed .brp shape members not serialized (recipe doc carries the construction recipe); baked Part::Feature solids carry a one-line shape summary decoded from their .brp
EXTERNAL_REF file=nakretka-rzymska.FCStd obj=Body
EXTERNAL_REF file=noga-gora.FCStd obj=Body
EXTERNAL_REF file=noga-dol.FCStd obj=Body

FEATURE [App::Link] Link  label="nakretka-rzymska"
  LinkPlacement = pos=(0.604474,0.0526819,2) rot=(0,0,1;0.086943rad)
  LinkedObject = -> <external nakretka-rzymska.FCStd>#Body
  Placement = pos=(0.604474,0.0526819,2) rot=(0,0,1;0.086943rad)
  SyncGroupVisibility = false
  _LinkVersion = 1
FEATURE [App::Link] Link001  label="noga-gora"
  LinkPlacement = pos=(0.604474,0.0526819,21) rot=(0,0,1;0.173886rad)
  LinkedObject = -> <external noga-gora.FCStd>#Body
  Placement = pos=(0.604474,0.0526819,21) rot=(0,0,1;0.173886rad)
  SyncGroupVisibility = false
  _LinkVersion = 1
FEATURE [App::Link] Link002  label="noga-dol"
  LinkPlacement = pos=(0,-5.76185e-06,-20) rot=(-1,0,0;3.14159rad)
  LinkedObject = -> <external noga-dol.FCStd>#Body
  Placement = pos=(0,-5.76185e-06,-20) rot=(-1,0,0;3.14159rad)
  SyncGroupVisibility = false
  _LinkVersion = 1
FEATURE [Part::FeaturePython] Parts  # WARN: FeaturePython — macro-defined, semantics opaque (R4)
  Group = -> [Link,Link001,Link002]
  GroupMode = 0
  _LinkVersion = 1
FEATURE [Part::FeaturePython] Assembly  label="regulacja-nogi"  # WARN: FeaturePython — macro-defined, semantics opaque (R4)
  AutoRelax = true
  BuildShape = 0
  Freeze = false
  Group = -> [Constraints,Elements,Parts]
  Verbose = false
  _LinkVersion = 1
  _SolverType = 1
  _Version = 1
FEATURE [App::FeaturePython] Constraints  # WARN: FeaturePython — macro-defined, semantics opaque (R4)
  Group = -> [Constraint,Constraint001,Constraint002,Constraint003]
  _LinkVersion = 1
  _Version = 1
FEATURE [App::FeaturePython] Elements  # WARN: FeaturePython — macro-defined, semantics opaque (R4)
  Group = -> [_Element,_Element001,_Element002,_Element003,_Element004,_Element005,Element,Element001,Element002]
  _LinkVersion = 1
FEATURE [App::FeaturePython] Constraint  label="Locked"  # WARN: FeaturePython — macro-defined, semantics opaque (R4)
  Disabled = false
  Group = -> [ElementLink]
  _ConstraintType = 0
  _LinkVersion = 0
  _Parent = -> Constraints
FEATURE [App::FeaturePython] ElementLink  label="_Element"  # link proxy (typed FeaturePython)
  LinkTransform = true
  LinkedObject = -> _Element
  _LinkVersion = 0
  _Parent = -> Constraint
FEATURE [Part::FeaturePython] _Element  # link proxy (typed FeaturePython)
  Detach = false
  LinkTransform = true
  LinkedObject = -> Link002 [Chamfer002.Face61]
  _LinkVersion = 0
  _Parent = -> Elements
FEATURE [App::FeaturePython] Constraint001  label="PlaneCoincident"  # WARN: FeaturePython — macro-defined, semantics opaque (R4)
  Angle = 0
  AnglePitch = 0
  AngleRoll = 0
  Cascade = false
  Disabled = false
  Group = -> [ElementLink001,ElementLink002]
  LockAngle = false
  Multiply = false
  Offset = -7
  OffsetX = 0
  OffsetY = 0
  _ConstraintType = 35
  _LinkVersion = 0
  _Parent = -> Constraints
FEATURE [App::FeaturePython] ElementLink001  label="_Element"  # link proxy (typed FeaturePython)
  LinkTransform = true
  LinkedObject = -> _Element
  _LinkVersion = 0
  _Parent = -> Constraint001
FEATURE [App::FeaturePython] ElementLink002  label="_Element001"  # link proxy (typed FeaturePython)
  LinkTransform = true
  LinkedObject = -> _Element001
  _LinkVersion = 0
  _Parent = -> Constraint001
FEATURE [Part::FeaturePython] _Element001  # link proxy (typed FeaturePython)
  Detach = false
  LinkTransform = true
  LinkedObject = -> Link [Fillet.Face2]
  _LinkVersion = 0
  _Parent = -> Elements
FEATURE [App::FeaturePython] Constraint002  label="PlaneCoincident001"  # WARN: FeaturePython — macro-defined, semantics opaque (R4)
  Angle = 0
  AnglePitch = 0
  AngleRoll = 0
  Cascade = false
  Disabled = false
  Group = -> [ElementLink003,ElementLink004]
  LockAngle = false
  Multiply = false
  Offset = 4
  OffsetX = 0
  OffsetY = 0
  _ConstraintType = 35
  _LinkVersion = 0
  _Parent = -> Constraints
FEATURE [App::FeaturePython] ElementLink003  label="_Element002"  # link proxy (typed FeaturePython)
  LinkTransform = true
  LinkedObject = -> _Element002
  _LinkVersion = 0
  _Parent = -> Constraint002
FEATURE [Part::FeaturePython] _Element002  # link proxy (typed FeaturePython)
  Detach = false
  LinkTransform = true
  LinkedObject = -> Link001 [Chamfer001.Face25]
  _LinkVersion = 0
  _Parent = -> Elements
FEATURE [App::FeaturePython] ElementLink004  label="_Element003"  # link proxy (typed FeaturePython)
  LinkTransform = true
  LinkedObject = -> _Element003
  _LinkVersion = 0
  _Parent = -> Constraint002
FEATURE [Part::FeaturePython] _Element003  # link proxy (typed FeaturePython)
  Detach = false
  LinkTransform = true
  LinkedObject = -> Link [Fillet.Face12]
  _LinkVersion = 0
  _Parent = -> Elements
FEATURE [App::FeaturePython] Constraint003  label="PointOnLine"  # WARN: FeaturePython — macro-defined, semantics opaque (R4)
  Disabled = false
  Group = -> [ElementLink005,ElementLink006]
  _ConstraintType = 4
  _LinkVersion = 0
  _Parent = -> Constraints
FEATURE [App::FeaturePython] ElementLink005  label="_Element004"  # link proxy (typed FeaturePython)
  LinkTransform = true
  LinkedObject = -> _Element004
  _LinkVersion = 0
  _Parent = -> Constraint003
FEATURE [Part::FeaturePython] _Element004  # link proxy (typed FeaturePython)
  Detach = false
  LinkTransform = true
  LinkedObject = -> Link001 [Chamfer001.Vertex29]
  _LinkVersion = 0
  _Parent = -> Elements
FEATURE [App::FeaturePython] ElementLink006  label="_Element005"  # link proxy (typed FeaturePython)
  LinkTransform = true
  LinkedObject = -> _Element005
  _LinkVersion = 0
  _Parent = -> Constraint003
FEATURE [Part::FeaturePython] _Element005  # link proxy (typed FeaturePython)
  Detach = false
  LinkTransform = true
  LinkedObject = -> Link002 [Chamfer002.Edge3]
  _LinkVersion = 0
  _Parent = -> Elements
FEATURE [Part::FeaturePython] Element  # link proxy (typed FeaturePython)
  Detach = false
  LinkTransform = true
  LinkedObject = -> Link002 [Chamfer002.Edge82]
  _LinkVersion = 0
  _Parent = -> Elements
FEATURE [Part::FeaturePython] Element001  # link proxy (typed FeaturePython)
  Detach = false
  LinkTransform = true
  LinkedObject = -> Link002 [Chamfer002.Vertex143]
  _LinkVersion = 0
  _Parent = -> Elements
FEATURE [Part::FeaturePython] Element002  # link proxy (typed FeaturePython)
  Detach = false
  LinkTransform = true
  LinkedObject = -> Link002 [Chamfer002.Face35]
  _LinkVersion = 0
  _Parent = -> Elements
---- part stopa.fcstd = doc fcstd_a06a6ed8e1db ----
FCSTD DOCUMENT  (FreeCAD 0.19R21911 +2545 (Git))
Label: stopa
License: All rights reserved
LicenseURL: http://en.wikipedia.org/wiki/All_rights_reserved
objects: Sketcher::SketchObject×1, PartDesign::Revolution×1, PartDesign::Body×1
note: 5 computed .brp shape members not serialized (recipe doc carries the construction recipe); baked Part::Feature solids carry a one-line shape summary decoded from their .brp

FEATURE [Sketcher::SketchObject] Sketch
  MapMode = 5
  Placement = pos=(0,0,0) rot=(1,0,0;1.5708rad)
  Support = -> [XZ_Plane]
  sketch-geometry (6):
    g0: LineSegment StartX=3 StartY=0 StartZ=0 EndX=15 EndY=0 EndZ=0
    g1: LineSegment StartX=15 StartY=0 StartZ=0 EndX=11 EndY=-30 EndZ=0
    g2: LineSegment StartX=11 StartY=-30 StartZ=0 EndX=6 EndY=-30 EndZ=0
    g3: LineSegment StartX=6 StartY=-30 StartZ=0 EndX=6 EndY=-10 EndZ=0
    g4: LineSegment StartX=6 StartY=-10 StartZ=0 EndX=3 EndY=-10 EndZ=0
    g5: LineSegment StartX=3 StartY=-10 StartZ=0 EndX=3 EndY=0 EndZ=0
  constraints (18):
    c: Horizontal(g0)
    c: Coincident(g0,g1)
    c: Coincident(g1,g2)
    c: Horizontal(g2)
    c: Coincident(g2,g3)
    c: Vertical(g3)
    c: Coincident(g3,g4)
    c: Horizontal(g4)
    c: Coincident(g4,g5)
    c: Coincident(g0,g5)
    c: Vertical(g5)
    c: DistanceX(g-1,g0) = 15
    c: DistanceX(g-1,g1) = 11
    c: DistanceY(g1,g0) = 30
    c: PointOnObject(g0,g-1)
    c: DistanceX(g2) = 6
    c: DistanceX(g4) = 3
    c: DistanceY(g3,g3) = 20
FEATURE [PartDesign::Revolution] Revolution
  AllowMultiFace = false
  Angle = 360
  Axis = (0,-1.035e-13,1)
  Base = (0,0,0)
  ClaimChildren = false
  Placement = pos=(0,0,0) rot=(1,0,0;1.5708rad)
  Profile = -> Sketch
  ReferenceAxis = -> Sketch [V_Axis]
  Reversed = true
  Suppress = false
FEATURE [PartDesign::Body] Body  label="stopa"
  ExportMode = 0
  Group = -> [Sketch,Revolution]
  Origin = -> Origin
  SingleSolid = true
  Tip = -> Revolution
  _ExportChildren = -> [Revolution]
  _GroupVersion = 1
---- part tulejka-sruby.FCStd = doc fcstd_06e5567c1162 ----
FCSTD DOCUMENT  (FreeCAD 2020.10.16R22739 +2665 (Git))
Label: tulejka-sruby
License: All rights reserved
LicenseURL: http://en.wikipedia.org/wiki/All_rights_reserved
objects: Sketcher::SketchObject×1, PartDesign::Pad×1, PartDesign::Chamfer×1, PartDesign::Body×1
note: 8 computed .brp shape members not serialized (recipe doc carries the construction recipe); baked Part::Feature solids carry a one-line shape summary decoded from their .brp

FEATURE [Sketcher::SketchObject] Sketch
  MapMode = 5
  Support = -> [XY_Plane]
  sketch-geometry (2):
    g0: Circle CenterX=0 CenterY=0 CenterZ=0 NormalX=0 NormalY=0 NormalZ=1 AngleXU=0 Radius=5.25
    g1: Circle CenterX=0 CenterY=0 CenterZ=0 NormalX=0 NormalY=0 NormalZ=1 AngleXU=0 Radius=7.25
  constraints (4):
    c: Coincident(g0,g-1)
    c: Coincident(g1,g0)
    c: Diameter(g0) = 10.5
    c: Diameter(g1) = 14.5
FEATURE [PartDesign::Pad] Pad
  ClaimChildren = false
  Direction = (1,1,1)
  Length = 17
  Length2 = 100
  NewSolid = false
  Profile = -> Sketch
  Suppress = false
  Type = 0
FEATURE [PartDesign::Chamfer] Chamfer
  Angle = 45
  Base = -> Pad [Edge3]
  BaseFeature = -> Pad
  ChamferType = 0
  FlipDirection = false
  NewSolid = false
  Size = 1
  Size2 = 1
  SupportTransform = true
  Suppress = false
FEATURE [PartDesign::Body] Body  label="tulejka-sruby"
  ExportMode = 0
  Group = -> [Sketch,Pad,Chamfer]
  Origin = -> Origin
  Tip = -> Chamfer
  _ExportChildren = -> [Pad,Chamfer]
  _GroupVersion = 1
---- part wieniec_mod1.FCStd = doc fcstd_3bf888632097 ----
FCSTD DOCUMENT  (FreeCAD 2020.10.16R22739 +2665 (Git))
Label: wieniec_mod1
License: All rights reserved
objects: Sketcher::SketchObject×4, PartDesign::Pocket×4, Part::FeaturePython×1, PartDesign::FeatureBase×1, PartDesign::PolarPattern×1, PartDesign::Body×1
note: 22 computed .brp shape members not serialized (recipe doc carries the construction recipe); baked Part::Feature solids carry a one-line shape summary decoded from their .brp

FEATURE [Part::FeaturePython] involutegear  # WARN: FeaturePython — macro-defined, semantics opaque (R4)
  backlash = 0
  beta = 0
  clearance = 0.25
  double_helix = false
  dw = 528
  head = 0
  height = 6
  module = 1
  numpoints = 6
  pressure_angle = 20
  properties_from_tool = true
  reversed_backlash = false
  shift = 0
  simple = false
  teeth = 528
  transverse_pitch = 3.14159
  undercut = false
FEATURE [PartDesign::FeatureBase] BaseFeature
  BaseFeature = -> involutegear
  NewSolid = false
  Suppress = false
FEATURE [Sketcher::SketchObject] Sketch
  MapMode = 5
  Placement = pos=(0,0,6) rot=(0,0,1;0rad)
  Support = -> [BaseFeature]
  sketch-geometry (1):
    g0: Circle CenterX=0 CenterY=0 CenterZ=0 NormalX=0 NormalY=0 NormalZ=1 AngleXU=0 Radius=260
  constraints (2):
    c: Coincident(g0,g-1)
    c: Diameter(g0) = 520
FEATURE [PartDesign::Pocket] Pocket
  BaseFeature = -> BaseFeature
  ClaimChildren = false
  Length = 2
  Length2 = 100
  NewSolid = false
  Profile = -> Sketch
  Suppress = false
  Type = 0
FEATURE [Sketcher::SketchObject] Sketch001
  MapMode = 5
  Placement = pos=(0,0,4) rot=(0,0,1;0rad)
  Support = -> [Pocket]
  sketch-geometry (1):
    g0: Circle CenterX=0 CenterY=0 CenterZ=0 NormalX=0 NormalY=0 NormalZ=1 AngleXU=0 Radius=250
  constraints (2):
    c: Coincident(g0,g-1)
    c: Diameter(g0) = 500
FEATURE [PartDesign::Pocket] Pocket001
  BaseFeature = -> Pocket
  ClaimChildren = false
  Length = 5
  Length2 = 100
  NewSolid = false
  Profile = -> Sketch001
  Suppress = false
  Type = 1
FEATURE [Sketcher::SketchObject] Sketch002
  MapMode = 5
  Placement = pos=(0,0,4) rot=(0,0,1;0rad)
  Support = -> [Pocket001]
  sketch-geometry (4):
    g0: ArcOfCircle CenterX=0 CenterY=254 CenterZ=0 NormalX=0 NormalY=0 NormalZ=1 AngleXU=0 Radius=2.1 StartAngle=3.14159 EndAngle=6.28319
    g1: ArcOfCircle CenterX=2e-16 CenterY=255 CenterZ=0 NormalX=0 NormalY=0 NormalZ=1 AngleXU=0 Radius=2.1 StartAngle=4.6e-15 EndAngle=3.14159
    g2: LineSegment StartX=2.1 StartY=254 StartZ=0 EndX=2.1 EndY=255 EndZ=0
    g3: LineSegment StartX=-2.1 StartY=254 StartZ=0 EndX=-2.1 EndY=255 EndZ=0
  constraints (10):
    c: Tangent(g0,g3) = 1.5708
    c: Tangent(g0,g2) = -1.5708
    c: Tangent(g2,g1) = -1.5708
    c: Tangent(g3,g1) = 1.5708
    c: Vertical(g2)
    c: Equal(g0,g1)
    c: PointOnObject(g0,g-2)
    c: Diameter(g0) = 4.2
    c: DistanceY(g2,g2) = 1
    c: DistanceY(g0) = 254
FEATURE [PartDesign::Pocket] Pocket002
  BaseFeature = -> Pocket001
  ClaimChildren = false
  Length = 5
  Length2 = 100
  NewSolid = false
  Profile = -> Sketch002
  Suppress = false
  Type = 1
FEATURE [PartDesign::PolarPattern] PolarPattern
  Angle = 360
  Axis = -> Sketch002 [N_Axis]
  BaseFeature = -> Pocket002
  CopyShape = false
  NewSolid = false
  Occurrences = 36
  OriginalSubs = -> [Pocket002]
  Originals = -> [Pocket002]
  SubTransform = true
  Suppress = false
FEATURE [Sketcher::SketchObject] Sketch003
  MapMode = 5
  Placement = pos=(0,0,6) rot=(0,0,1;0rad)
  Support = -> [PolarPattern]
  sketch-geometry (3):
    g0: LineSegment StartX=-26.7392 StartY=298.806 StartZ=0 EndX=3.6e-15 EndY=0 EndZ=0
    g1: LineSegment StartX=0 StartY=0 StartZ=0 EndX=213.39 EndY=210.866 EndZ=0
    g2: ArcOfCircle CenterX=0 CenterY=0 CenterZ=0 NormalX=0 NormalY=0 NormalZ=1 AngleXU=0 Radius=300 StartAngle=1.66005 EndAngle=7.06263
  constraints (8):
    c: Coincident(g0,g-1)
    c: Coincident(g1,g0)
    c: Angle(g-2,g0) = 0.0892492
    c: Coincident(g2,g0)
    c: Coincident(g2,g0)
    c: Coincident(g2,g1)
    c: Distance(g0) = 300
    c: Angle(g1,g0) = 0.880597
FEATURE [PartDesign::Pocket] Pocket003
  BaseFeature = -> PolarPattern
  ClaimChildren = false
  Length = 5
  Length2 = 100
  NewSolid = false
  Profile = -> Sketch003
  Suppress = false
  Type = 1
FEATURE [PartDesign::Body] Body  label="wieniec"
  BaseFeature = -> involutegear
  ExportMode = 0
  Group = -> [BaseFeature,Sketch,Pocket,Sketch001,Pocket001,Sketch002,Pocket002,PolarPattern,Sketch003,Pocket003]
  Origin = -> Origin
  Tip = -> Pocket003
  _ExportChildren = -> [BaseFeature,Pocket,Pocket001,Pocket002,PolarPattern,Pocket003]
  _GroupVersion = 1
